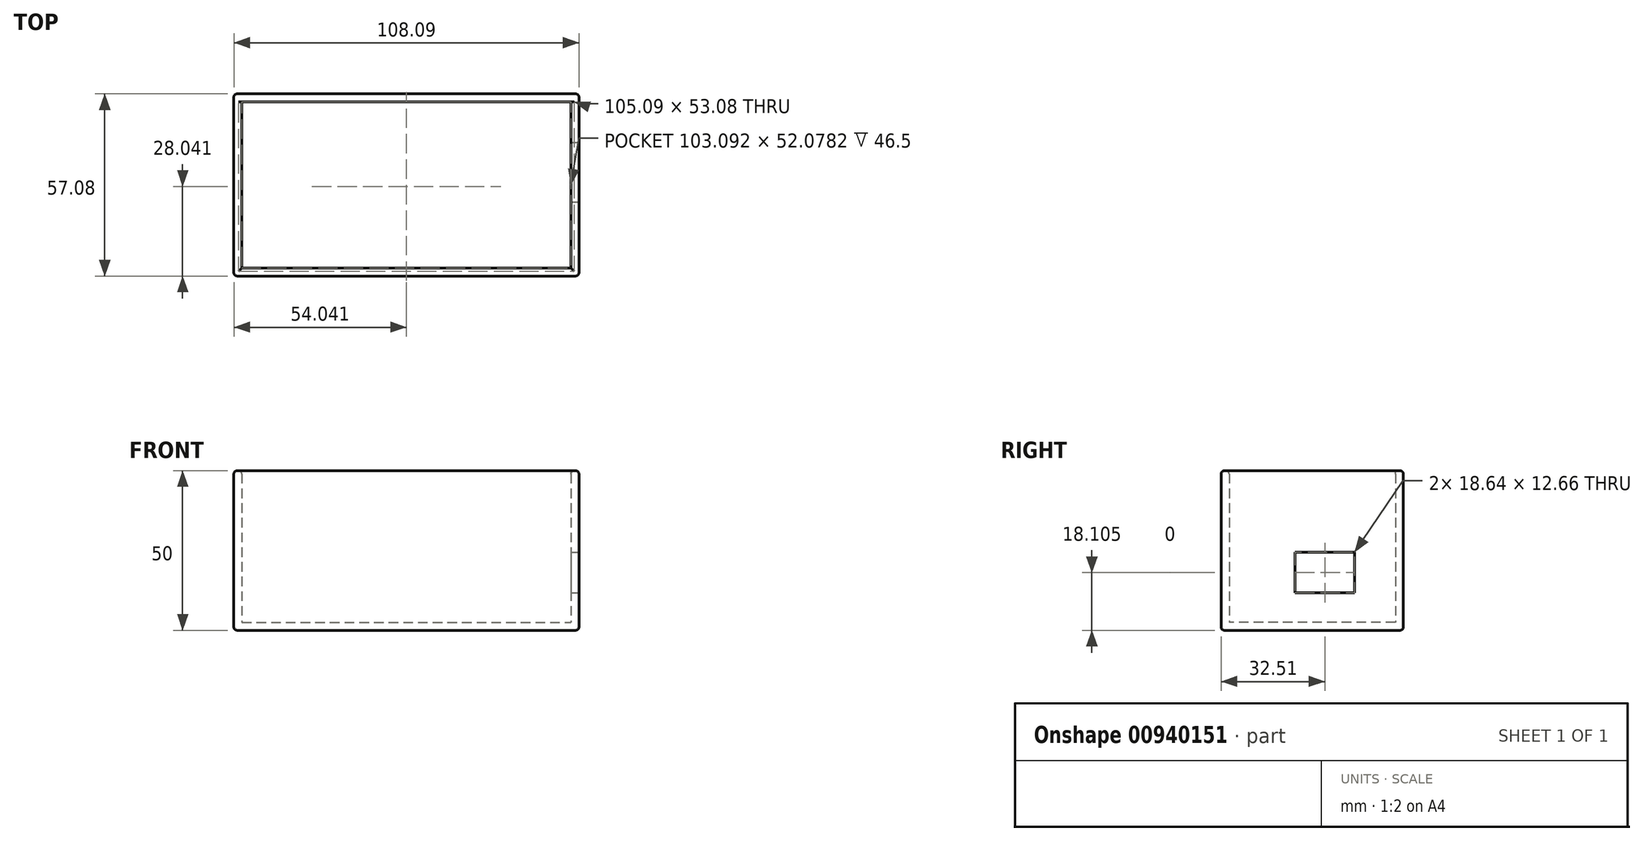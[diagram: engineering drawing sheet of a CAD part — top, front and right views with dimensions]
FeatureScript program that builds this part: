
annotation { "Feature Type Name" : "Feature", "Feature Type Description" : "" }
export const myFeature = defineFeature(function(context is Context, id is Id, definition is map)
    precondition{}
    {
        {
            var Q0;
            Q0=qCreatedBy(makeId("Top.planeOp"),FACE);
            var sketch = newSketch(context, id + "F0", { "sketchPlane" : qUnion([Q0])});
            skLineSegment(sketch, "E0.bottom", {"start": v(-61.8, 33.9) * mm, "end": v(46.29, 33.9) * mm});
            skLineSegment(sketch, "E0.top", {"start": v(-61.8, -23.19) * mm, "end": v(46.29, -23.19) * mm});
            skLineSegment(sketch, "E0.left", {"start": v(-61.8, 33.9) * mm, "end": v(-61.8, -23.19) * mm});
            skLineSegment(sketch, "E0.right", {"start": v(46.29, 33.9) * mm, "end": v(46.29, -23.19) * mm});
            skSolve(sketch);
        }
        {
            var Q0;
            Q0 = qSketchRegion(id + "F0", true);
            var Q1;
            Q1=makeQuery(id+"F0.imprint","IMPRINT",FACE,{"disambiguationData":[TD([[makeQuery(id+"F0.imprint","IMPRINT",EDGE,{"derivedFrom":sQuery(id+"F0.wireOp",EDGE,"E0.bottom")}),-1.0]])]});
            extrude(context, id + "F1", {"entities" : qUnion([Q0, Q1]), "depth" : 50 * mm, "offsetDistance" : 25 * mm});
        }
        {
            var Q0;
            Q0=makeQuery(id+"F1.opExtrude","CAP_FACE",FACE,{"disambiguationData":[OSD([sQuery(id+"F0.wireOp",EDGE,"E0.bottom"),sQuery(id+"F0.wireOp",EDGE,"E0.top"),sQuery(id+"F0.wireOp",EDGE,"E0.left"),sQuery(id+"F0.wireOp",EDGE,"E0.right")])],"isStart":false});
            shell(context, id + "F2", {"entities" : qUnion([Q0]), "thickness" : 2.5 * mm});
        }
        {
            var Q0;
            Q0=makeQuery(id+"F1.opExtrude","CAP_EDGE",EDGE,{"disambiguationData":[OSD([sQuery(id+"F0.wireOp",EDGE,"E0.top")])],"isStart":false});
            var Q1;
            Q1=makeQuery(id+"F1.opExtrude","SWEPT_EDGE",EDGE,{"disambiguationData":[OSD([sQuery(id+"F0.wireOp",EDGE,"E0.top"),sQuery(id+"F0.wireOp",EDGE,"E0.left")])]});
            var Q2;
            {var subQ0=sQuery(id+"F0.wireOp",EDGE,"E0.top");Q2=makeQuery(id+"F2.opShell","OFFSET_EDGE",EDGE,{"disambiguationData":[OSD([subQ0]),TDD([makeQuery(id+"F1.opExtrude","CAP_EDGE",EDGE,{"disambiguationData":[OSD([subQ0])],"isStart":false})])]});}
            var Q3;
            {var subQ0=sQuery(id+"F0.wireOp",EDGE,"E0.left");Q3=makeQuery(id+"F2.opShell","OFFSET_EDGE",EDGE,{"disambiguationData":[OSD([subQ0]),TDD([makeQuery(id+"F1.opExtrude","CAP_EDGE",EDGE,{"disambiguationData":[OSD([subQ0])],"isStart":false})])]});}
            var Q4;
            Q4=makeQuery(id+"F1.opExtrude","CAP_EDGE",EDGE,{"disambiguationData":[OSD([sQuery(id+"F0.wireOp",EDGE,"E0.left")])],"isStart":false});
            var Q5;
            Q5=makeQuery(id+"F1.opExtrude","CAP_EDGE",EDGE,{"disambiguationData":[OSD([sQuery(id+"F0.wireOp",EDGE,"E0.top")])],"isStart":true});
            var Q6;
            Q6=makeQuery(id+"F1.opExtrude","SWEPT_EDGE",EDGE,{"disambiguationData":[OSD([sQuery(id+"F0.wireOp",EDGE,"E0.top"),sQuery(id+"F0.wireOp",EDGE,"E0.right")])]});
            var Q7;
            {var subQ0=sQuery(id+"F0.wireOp",EDGE,"E0.right");Q7=makeQuery(id+"F2.opShell","OFFSET_EDGE",EDGE,{"disambiguationData":[OSD([subQ0]),TDD([makeQuery(id+"F1.opExtrude","CAP_EDGE",EDGE,{"disambiguationData":[OSD([subQ0])],"isStart":false})])]});}
            var Q8;
            Q8=makeQuery(id+"F1.opExtrude","CAP_EDGE",EDGE,{"disambiguationData":[OSD([sQuery(id+"F0.wireOp",EDGE,"E0.right")])],"isStart":false});
            var Q9;
            Q9=makeQuery(id+"F1.opExtrude","CAP_EDGE",EDGE,{"disambiguationData":[OSD([sQuery(id+"F0.wireOp",EDGE,"E0.right")])],"isStart":true});
            fillet(context, id + "F3", {"entities" : qUnion([Q0, Q1, Q2, Q3, Q4, Q5, Q6, Q7, Q8, Q9]), "radius" : 1 * mm, "tangentPropagation" : true, "allowEdgeOverflow" : false});
        }
        {
            var Q0;
            Q0=makeQuery(id+"F1.opExtrude","SWEPT_EDGE",EDGE,{"disambiguationData":[OSD([sQuery(id+"F0.wireOp",EDGE,"E0.bottom"),sQuery(id+"F0.wireOp",EDGE,"E0.right")])]});
            var Q1;
            Q1=makeQuery(id+"F1.opExtrude","CAP_EDGE",EDGE,{"disambiguationData":[OSD([sQuery(id+"F0.wireOp",EDGE,"E0.bottom")])],"isStart":false});
            var Q2;
            Q2=makeQuery(id+"F1.opExtrude","CAP_EDGE",EDGE,{"disambiguationData":[OSD([sQuery(id+"F0.wireOp",EDGE,"E0.left")])],"isStart":true});
            fillet(context, id + "F4", {"entities" : qUnion([Q0, Q1, Q2]), "radius" : 1 * mm, "tangentPropagation" : true, "allowEdgeOverflow" : false});
        }
        {
            var Q0;
            Q0=makeQuery(id+"F1.opExtrude","SWEPT_FACE",FACE,{"disambiguationData":[OSD([sQuery(id+"F0.wireOp",EDGE,"E0.right")])]});
            var sketch = newSketch(context, id + "F5", { "sketchPlane" : qUnion([Q0])});
            skLineSegment(sketch, "E1.bottom", {"start": v(0, 24.44) * mm, "end": v(18.64, 24.44) * mm});
            skLineSegment(sketch, "E1.top", {"start": v(0, 11.77) * mm, "end": v(18.64, 11.77) * mm});
            skLineSegment(sketch, "E1.left", {"start": v(0, 24.44) * mm, "end": v(0, 11.77) * mm});
            skLineSegment(sketch, "E1.right", {"start": v(18.64, 24.44) * mm, "end": v(18.64, 11.77) * mm});
            skSolve(sketch);
        }
        {
            var Q0;
            Q0=makeQuery(id+"F5.imprint","IMPRINT",FACE,{"disambiguationData":[TD([[makeQuery(id+"F5.imprint","IMPRINT",EDGE,{"derivedFrom":sQuery(id+"F5.wireOp",EDGE,"E1.bottom")}),-1.0]])]});
            extrude(context, id + "F6", {"entities" : qUnion([Q0]), "operationType" : NewBodyOperationType.REMOVE, "oppositeDirection" : true, "depth" : 25 * mm, "offsetDistance" : 25 * mm});
        }
    });
